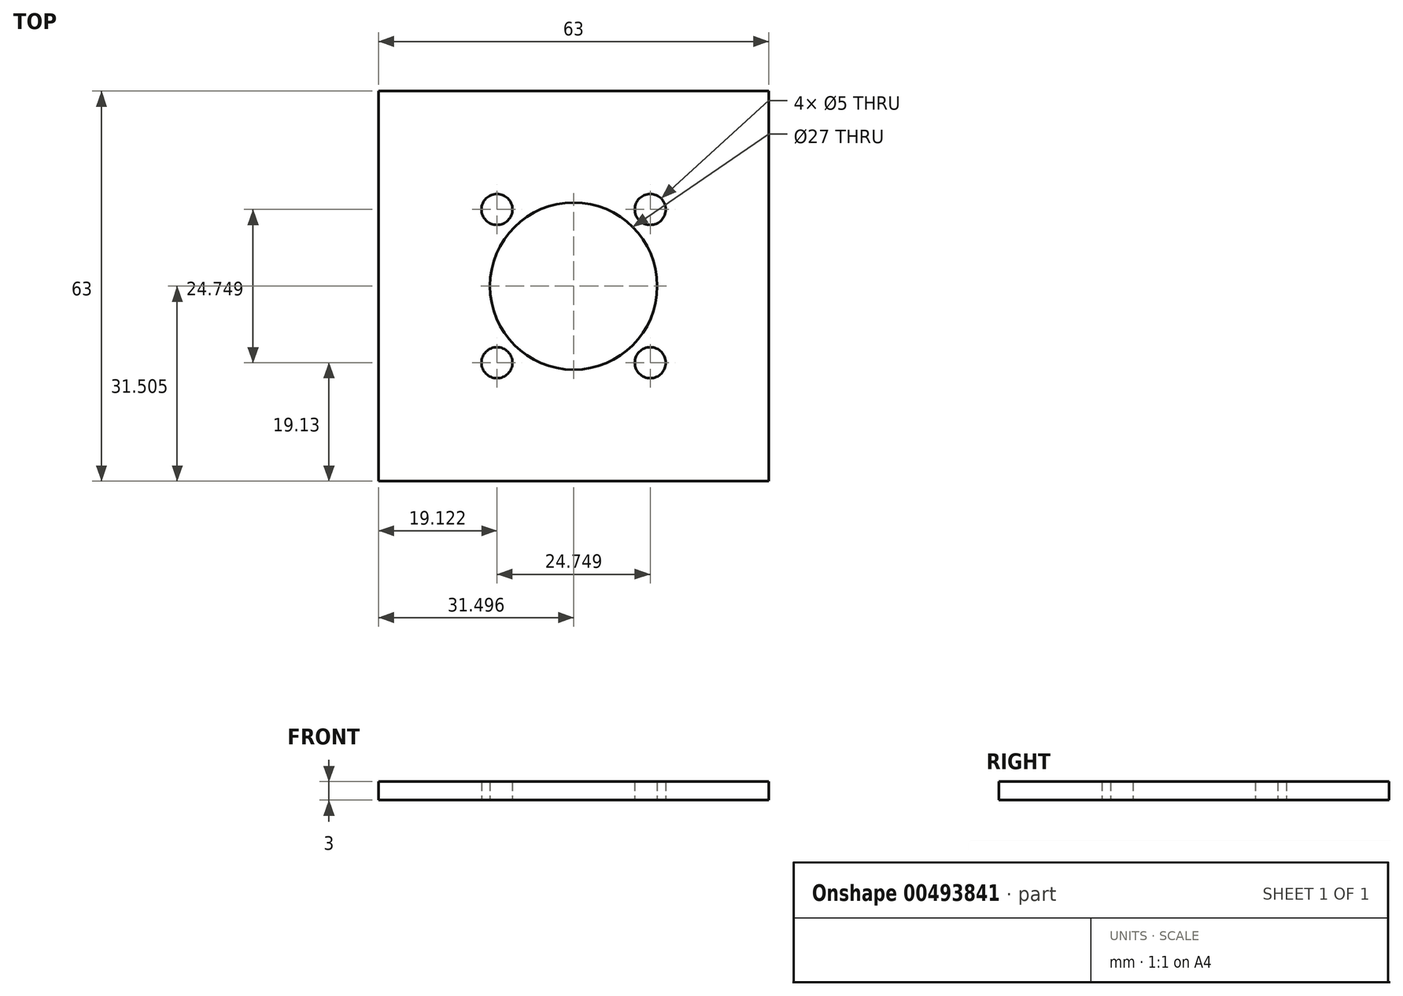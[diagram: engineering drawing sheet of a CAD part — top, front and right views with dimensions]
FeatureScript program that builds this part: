
annotation { "Feature Type Name" : "Feature", "Feature Type Description" : "" }
export const myFeature = defineFeature(function(context is Context, id is Id, definition is map)
    precondition{}
    {
        {
            var Q0;
            Q0=qCreatedBy(makeId("Top.planeOp"),FACE);
            var sketch = newSketch(context, id + "F0", { "sketchPlane" : qUnion([Q0])});
            skLineSegment(sketch, "E0.bottom", {"start": v(-25.81, 25.53) * mm, "end": v(37.19, 25.53) * mm});
            skLineSegment(sketch, "E0.top", {"start": v(-25.81, -37.47) * mm, "end": v(37.19, -37.47) * mm});
            skLineSegment(sketch, "E0.left", {"start": v(-25.81, 25.53) * mm, "end": v(-25.81, -37.47) * mm});
            skLineSegment(sketch, "E0.right", {"start": v(37.19, 25.53) * mm, "end": v(37.19, -37.47) * mm});
            skCircle(sketch, "E1", {"center": v(5.69, -5.97) * mm, "radius": 13.5 * mm});
            skCircle(sketch, "E2", {"center": v(-6.69, 6.4) * mm, "radius": 2.5 * mm});
            skCircle(sketch, "E3", {"center": v(18.06, 6.4) * mm, "radius": 2.5 * mm});
            skCircle(sketch, "E4", {"center": v(18.06, -18.34) * mm, "radius": 2.5 * mm});
            skCircle(sketch, "E5", {"center": v(-6.69, -18.34) * mm, "radius": 2.5 * mm});
            skSolve(sketch);
        }
        {
            var Q0;
            Q0 = qSketchRegion(id + "F0", true);
            extrude(context, id + "F1", {"entities" : qUnion([Q0]), "depth" : 3 * mm});
        }
    });
